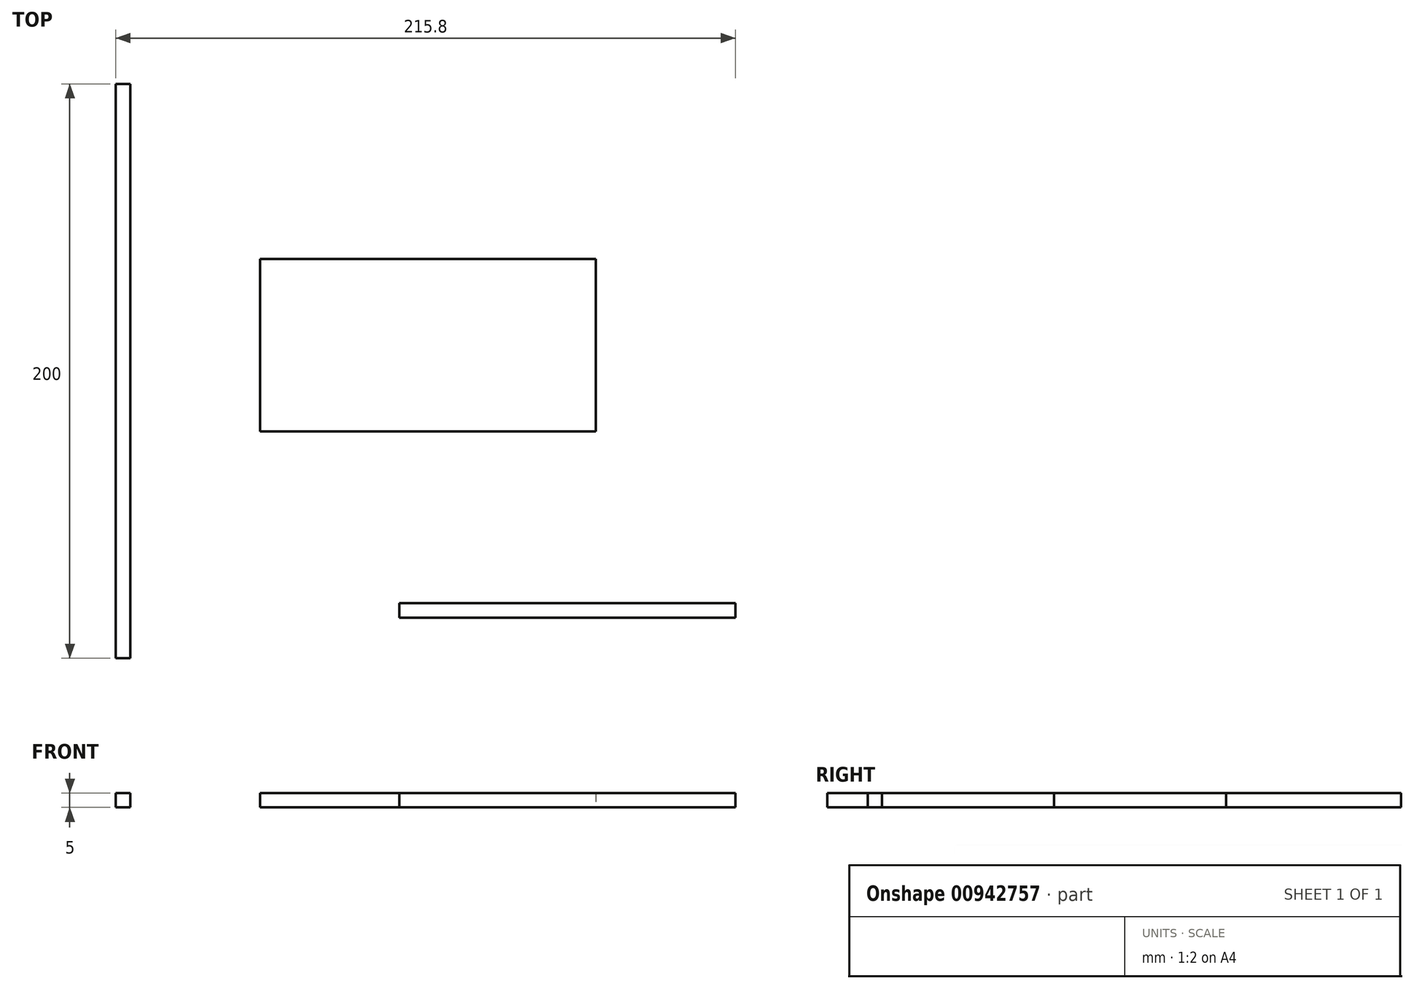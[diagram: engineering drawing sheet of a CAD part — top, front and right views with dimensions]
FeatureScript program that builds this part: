
annotation { "Feature Type Name" : "Feature", "Feature Type Description" : "" }
export const myFeature = defineFeature(function(context is Context, id is Id, definition is map)
    precondition{}
    {
        {
            var Q0;
            Q0=qCreatedBy(makeId("Top.planeOp"),FACE);
            var sketch = newSketch(context, id + "F0", { "sketchPlane" : qUnion([Q0])});
            skLineSegment(sketch, "E0.bottom", {"start": v(58.5, 30) * mm, "end": v(-58.5, 30) * mm});
            skLineSegment(sketch, "E0.top", {"start": v(58.5, -30) * mm, "end": v(-58.5, -30) * mm});
            skLineSegment(sketch, "E0.left", {"start": v(58.5, 30) * mm, "end": v(58.5, -30) * mm});
            skLineSegment(sketch, "E0.right", {"start": v(-58.5, 30) * mm, "end": v(-58.5, -30) * mm});
            skPoint(sketch, "E0.middle", {"position": v(0, 0) * mm});
            skSolve(sketch);
        }
        {
            var Q0;
            Q0 = qSketchRegion(id + "F0", true);
            extrude(context, id + "F1", {"entities" : qUnion([Q0]), "depth" : 5 * mm, "offsetDistance" : 25 * mm});
        }
        {
            var Q0;
            Q0=qCreatedBy(makeId("Top.planeOp"),FACE);
            var sketch = newSketch(context, id + "F2", { "sketchPlane" : qUnion([Q0])});
            skLineSegment(sketch, "E1.bottom", {"start": v(125, 108.5) * mm, "end": v(-125, 108.5) * mm});
            skLineSegment(sketch, "E1.top", {"start": v(125, -108.5) * mm, "end": v(-125, -108.5) * mm});
            skLineSegment(sketch, "E1.left", {"start": v(125, 108.5) * mm, "end": v(125, -108.5) * mm});
            skLineSegment(sketch, "E1.right", {"start": v(-125, 108.5) * mm, "end": v(-125, -108.5) * mm});
            skPoint(sketch, "E1.middle", {"position": v(0, 0) * mm});
            skSolve(sketch);
        }
        {
            var Q0;
            Q0=makeQuery(id+"F2.imprint","IMPRINT",FACE,{"disambiguationData":[TD([[makeQuery(id+"F2.imprint","IMPRINT",EDGE,{"derivedFrom":sQuery(id+"F2.wireOp",EDGE,"E1.bottom")}),1.0]])]});
            var sketch = newSketch(context, id + "F3", { "sketchPlane" : qUnion([Q0])});
            skLineSegment(sketch, "E2.bottom", {"start": v(-108.76, -109) * mm, "end": v(-103.76, -109) * mm});
            skLineSegment(sketch, "E2.top", {"start": v(-108.76, 91) * mm, "end": v(-103.76, 91) * mm});
            skLineSegment(sketch, "E2.left", {"start": v(-108.76, -109) * mm, "end": v(-108.76, 91) * mm});
            skLineSegment(sketch, "E2.right", {"start": v(-103.76, -109) * mm, "end": v(-103.76, 91) * mm});
            skSolve(sketch);
        }
        {
            var Q0;
            Q0 = qSketchRegion(id + "F3", true);
            extrude(context, id + "F4", {"entities" : qUnion([Q0]), "depth" : 5 * mm, "offsetDistance" : 25 * mm});
        }
        {
            var Q0;
            Q0=makeQuery(id+"F2.imprint","IMPRINT",FACE,{"disambiguationData":[TD([[makeQuery(id+"F2.imprint","IMPRINT",EDGE,{"derivedFrom":sQuery(id+"F2.wireOp",EDGE,"E1.bottom")}),1.0]])]});
            var sketch = newSketch(context, id + "F5", { "sketchPlane" : qUnion([Q0])});
            skLineSegment(sketch, "E3.bottom", {"start": v(-9.96, -94.9) * mm, "end": v(107.04, -94.9) * mm});
            skLineSegment(sketch, "E3.top", {"start": v(-9.96, -89.9) * mm, "end": v(107.04, -89.9) * mm});
            skLineSegment(sketch, "E3.left", {"start": v(-9.96, -94.9) * mm, "end": v(-9.96, -89.9) * mm});
            skLineSegment(sketch, "E3.right", {"start": v(107.04, -94.9) * mm, "end": v(107.04, -89.9) * mm});
            skSolve(sketch);
        }
        {
            var Q0;
            Q0 = qSketchRegion(id + "F5", true);
            extrude(context, id + "F6", {"entities" : qUnion([Q0]), "depth" : 5 * mm, "offsetDistance" : 25 * mm});
        }
    });
